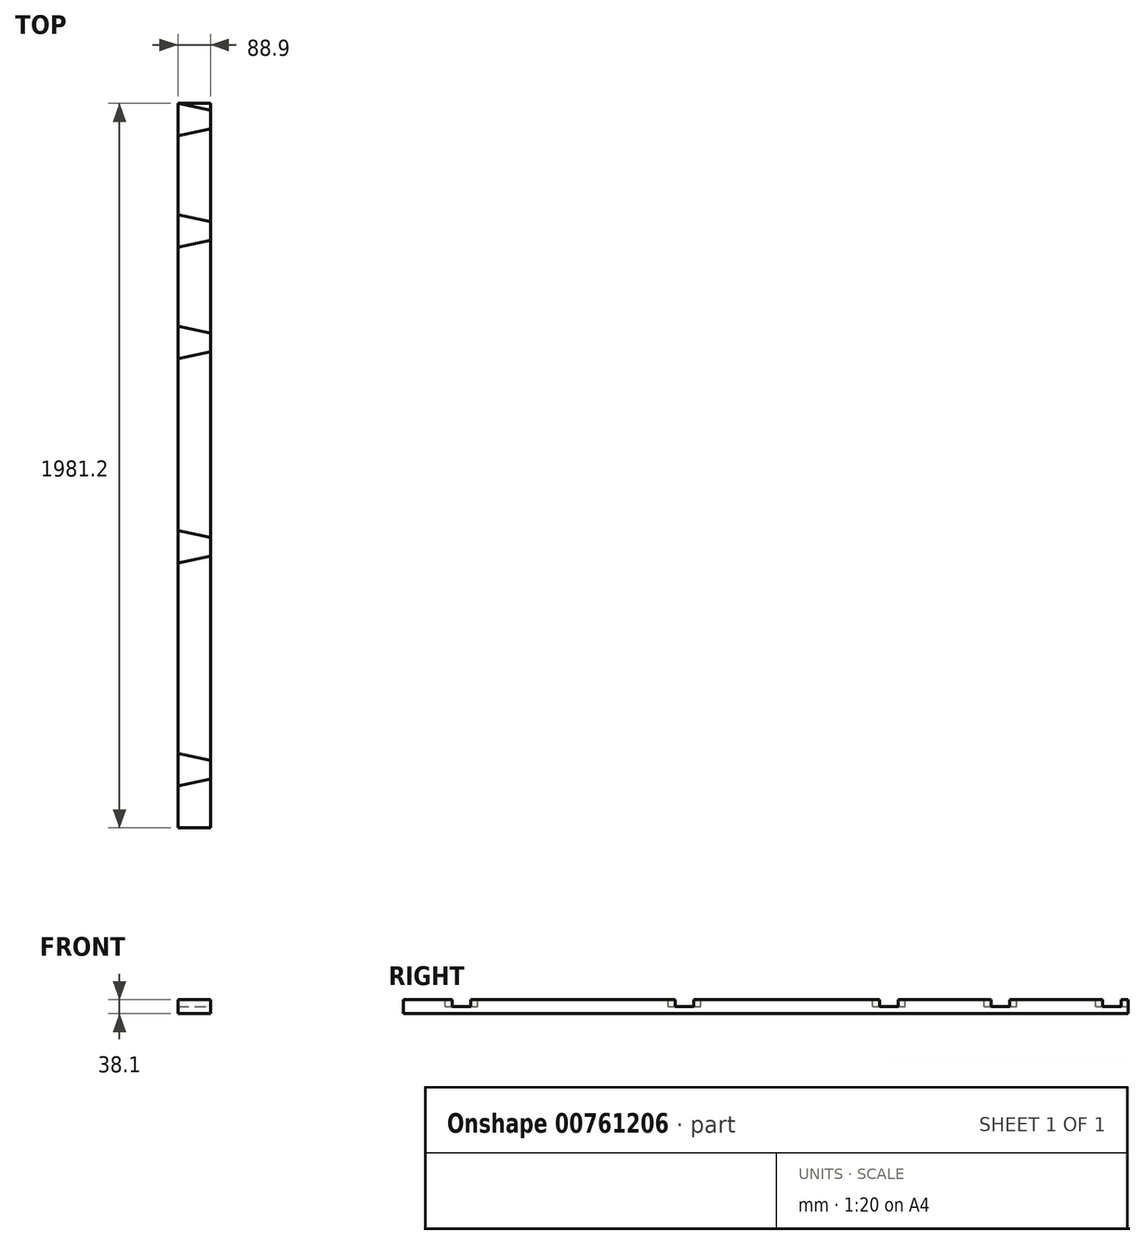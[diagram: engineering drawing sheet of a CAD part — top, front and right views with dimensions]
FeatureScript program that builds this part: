
annotation { "Feature Type Name" : "Feature", "Feature Type Description" : "" }
export const myFeature = defineFeature(function(context is Context, id is Id, definition is map)
    precondition{}
    {
        {
            var Q0;
            Q0=qCreatedBy(makeId("Front.planeOp"),FACE);
            var sketch = newSketch(context, id + "F0", { "sketchPlane" : qUnion([Q0])});
            skLineSegment(sketch, "E0.bottom", {"start": v(44.45, 19.05) * mm, "end": v(-44.45, 19.05) * mm});
            skLineSegment(sketch, "E0.top", {"start": v(44.45, -19.05) * mm, "end": v(-44.45, -19.05) * mm});
            skLineSegment(sketch, "E0.left", {"start": v(44.45, 19.05) * mm, "end": v(44.45, -19.05) * mm});
            skLineSegment(sketch, "E0.right", {"start": v(-44.45, 19.05) * mm, "end": v(-44.45, -19.05) * mm});
            skPoint(sketch, "E0.middle", {"position": v(0, 0) * mm});
            skSolve(sketch);
        }
        {
            var Q0;
            Q0 = qSketchRegion(id + "F0", true);
            extrude(context, id + "F1", {"entities" : qUnion([Q0]), "depth" : 1981.2 * mm, "offsetDistance" : 25.4 * mm});
        }
        {
            var Q0;
            Q0=makeQuery(id+"F1.opExtrude","SWEPT_FACE",FACE,{"disambiguationData":[OSD([sQuery(id+"F0.wireOp",EDGE,"E0.bottom")])]});
            var sketch = newSketch(context, id + "F2", { "sketchPlane" : qUnion([Q0])});
            skLineSegment(sketch, "E1", {"start": v(-44.45, 0) * mm, "end": v(-44.45, -88.9) * mm});
            skLineSegment(sketch, "E2", {"start": v(-44.45, -88.9) * mm, "end": v(44.45, -69.85) * mm});
            skLineSegment(sketch, "E3", {"start": v(44.45, -69.85) * mm, "end": v(44.45, -19.05) * mm});
            skLineSegment(sketch, "E4", {"start": v(44.45, -19.05) * mm, "end": v(-44.45, 0) * mm});
            skLineSegment(sketch, "E5", {"start": v(-44.45, -304.8) * mm, "end": v(-44.45, -393.7) * mm});
            skLineSegment(sketch, "E6", {"start": v(-44.45, -393.7) * mm, "end": v(44.45, -374.65) * mm});
            skLineSegment(sketch, "E7", {"start": v(44.45, -374.65) * mm, "end": v(44.45, -323.85) * mm});
            skLineSegment(sketch, "E8", {"start": v(44.45, -323.85) * mm, "end": v(-44.45, -304.8) * mm});
            skLineSegment(sketch, "E9", {"start": v(-44.45, -609.6) * mm, "end": v(-44.45, -698.5) * mm});
            skLineSegment(sketch, "E10", {"start": v(-44.45, -698.5) * mm, "end": v(44.45, -679.45) * mm});
            skLineSegment(sketch, "E11", {"start": v(44.45, -679.45) * mm, "end": v(44.45, -628.65) * mm});
            skLineSegment(sketch, "E12", {"start": v(44.45, -628.65) * mm, "end": v(-44.45, -609.6) * mm});
            skLineSegment(sketch, "E13", {"start": v(-44.45, -1168.4) * mm, "end": v(-44.45, -1257.3) * mm});
            skLineSegment(sketch, "E14", {"start": v(-44.45, -1257.3) * mm, "end": v(44.45, -1238.25) * mm});
            skLineSegment(sketch, "E15", {"start": v(44.45, -1238.25) * mm, "end": v(44.45, -1187.45) * mm});
            skLineSegment(sketch, "E16", {"start": v(44.45, -1187.45) * mm, "end": v(-44.45, -1168.4) * mm});
            skLineSegment(sketch, "E17", {"start": v(-44.45, -1778) * mm, "end": v(-44.45, -1866.9) * mm});
            skLineSegment(sketch, "E18", {"start": v(-44.45, -1866.9) * mm, "end": v(44.45, -1847.85) * mm});
            skLineSegment(sketch, "E19", {"start": v(44.45, -1847.85) * mm, "end": v(44.45, -1797.05) * mm});
            skLineSegment(sketch, "E20", {"start": v(44.45, -1797.05) * mm, "end": v(-44.45, -1778) * mm});
            skSolve(sketch);
        }
        {
            var Q0;
            Q0 = qSketchRegion(id + "F2", true);
            var Q1;
            Q1=makeQuery(id+"F2.imprint","IMPRINT",FACE,{"disambiguationData":[TD([[makeQuery(id+"F2.imprint","IMPRINT",EDGE,{"derivedFrom":sQuery(id+"F2.wireOp",EDGE,"E1")}),-1.0]])]});
            extrude(context, id + "F3", {"entities" : qUnion([Q0, Q1]), "operationType" : NewBodyOperationType.REMOVE, "oppositeDirection" : true, "depth" : 19.05 * mm, "offsetDistance" : 25.4 * mm});
        }
    });
